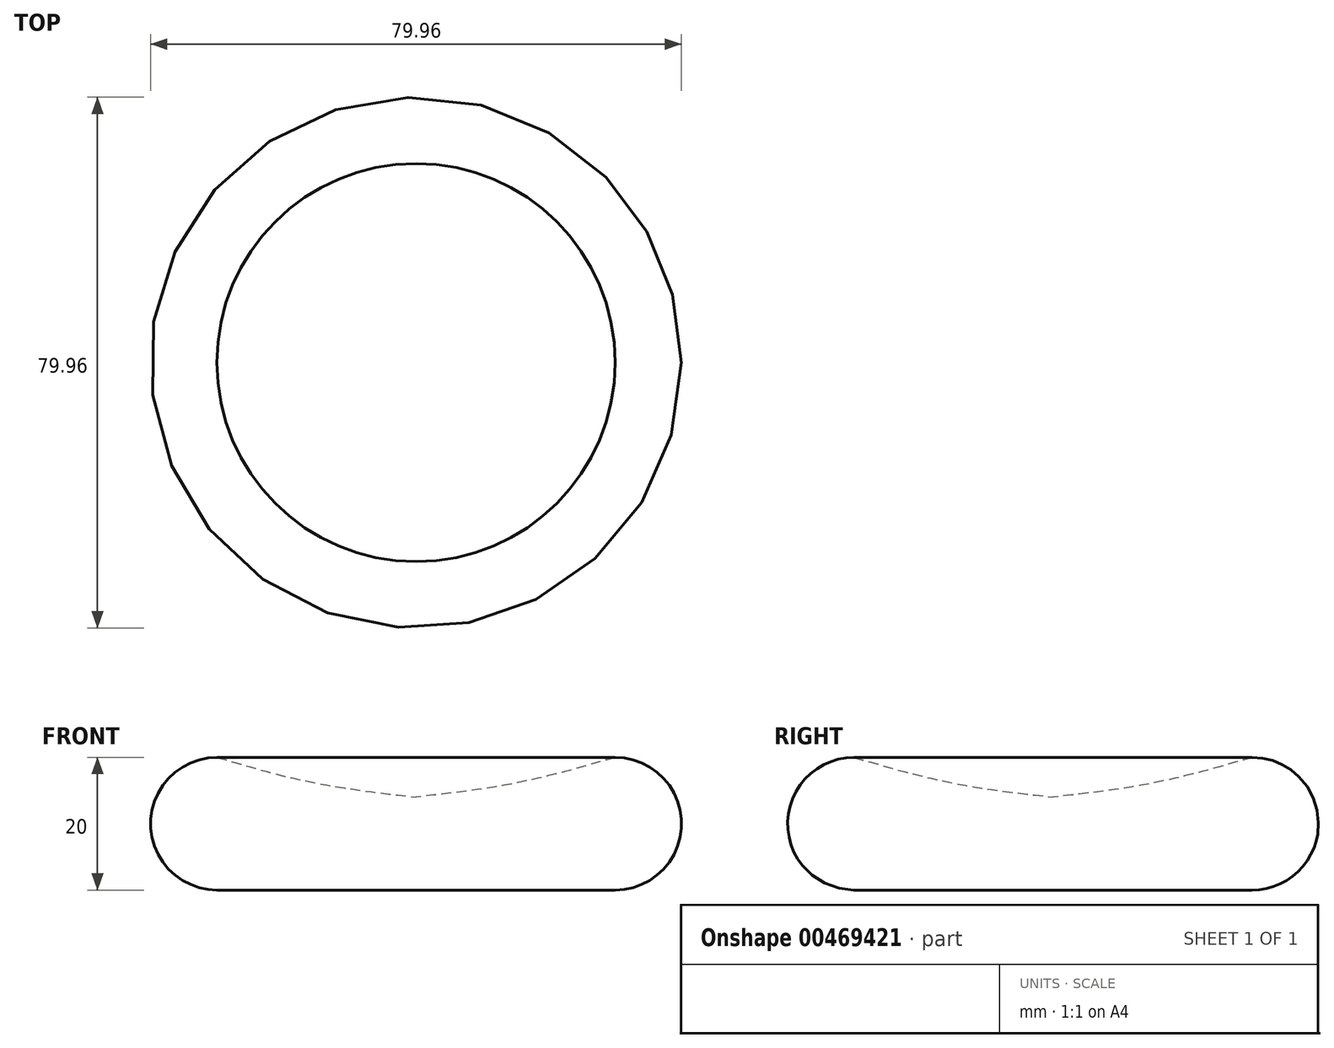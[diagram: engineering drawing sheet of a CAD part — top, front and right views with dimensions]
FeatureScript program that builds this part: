
annotation { "Feature Type Name" : "Feature", "Feature Type Description" : "" }
export const myFeature = defineFeature(function(context is Context, id is Id, definition is map)
    precondition{}
    {
        {
            var Q0;
            Q0=qCreatedBy(makeId("Front.planeOp"),FACE);
            var sketch = newSketch(context, id + "F0", { "sketchPlane" : qUnion([Q0])});
            skLineSegment(sketch, "E0", {"start": v(0, 0) * mm, "end": v(-30, 0) * mm});
            skArc(sketch, "E1", {"start": v(-30, 20) * mm, "mid": v(-39.98, 10) * mm, "end": v(-30, 0) * mm});
            skPoint(sketch, "E2.orphan", {"position": v(-40, 0) * mm});
            skFitSpline(sketch, "E3", {"points": [v(-30, 20) * mm, v(-15.74, 16.26) * mm, v(0, 14) * mm], "startDerivative": vector(28.63, -8.42) * mm, "endDerivative": vector(31.36, -3.62) * mm});
            skLineSegment(sketch, "E4", {"start": v(0, 14) * mm, "end": v(0, 0) * mm});
            skLineSegment(sketch, "E5", {"start": v(0, 23.04) * mm, "end": v(0, 19.19) * mm});
            skSolve(sketch);
        }
        {
            var Q0;
            Q0 = qSketchRegion(id + "F0", true);
            var Q1;
            Q1=sQuery(id+"F0.wireOp",EDGE,"E5");
            revolve(context, id + "F1", {"entities" : qUnion([Q0]), "axis" : qUnion([Q1]), "revolveType" : RevolveType.FULL});
        }
    });
